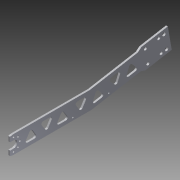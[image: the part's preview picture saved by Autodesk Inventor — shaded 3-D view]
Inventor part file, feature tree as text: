
AUTODESK INVENTOR PART (.ipt)
format: ipt  version: 2013 (Build 170138000, 138)  size: 2,888,192 bytes
history: native  units: mm
features: sketch x8, hole x5, extrude x3, other x2, pattern_circular x1, fillet x1
ambient origin geometry x8: Origin, YZ Plane, XZ Plane, XY Plane, X Axis, Y Axis, Z Axis, Center Point
feature tree (20):
  other  "ソリッド1"
  extrude  "押し出し1"  Depth=20.0mm
  hole  "穴2"  [1 undecoded]
  extrude  "押し出し2"  Depth=10.0mm
  hole  "穴3"  [1 undecoded]
  hole  "穴4"  [1 undecoded]
  pattern_circular  "円形状パターン3"  [2 undecoded]
  hole  "穴5"  [1 undecoded]
  hole  "穴6"  [1 undecoded]
  extrude  "押し出し4"  Depth=4.0mm
  fillet  "フィレット1"  Radius=170.0mm
  sketch  "スケッチ2"
  sketch  "スケッチ4"
  sketch  "スケッチ5"
  sketch  "スケッチ6"
  sketch  "スケッチ7"
  sketch  "スケッチ8"
  sketch  "スケッチ11"
  sketch  "スケッチ13"
  other  "断面エッジを投影1"
note: 7 required parameter values undecoded (feature->parameter linkage not recoverable at this tier; creation-order binding heuristic only, values carry confidence <= 0.55)
